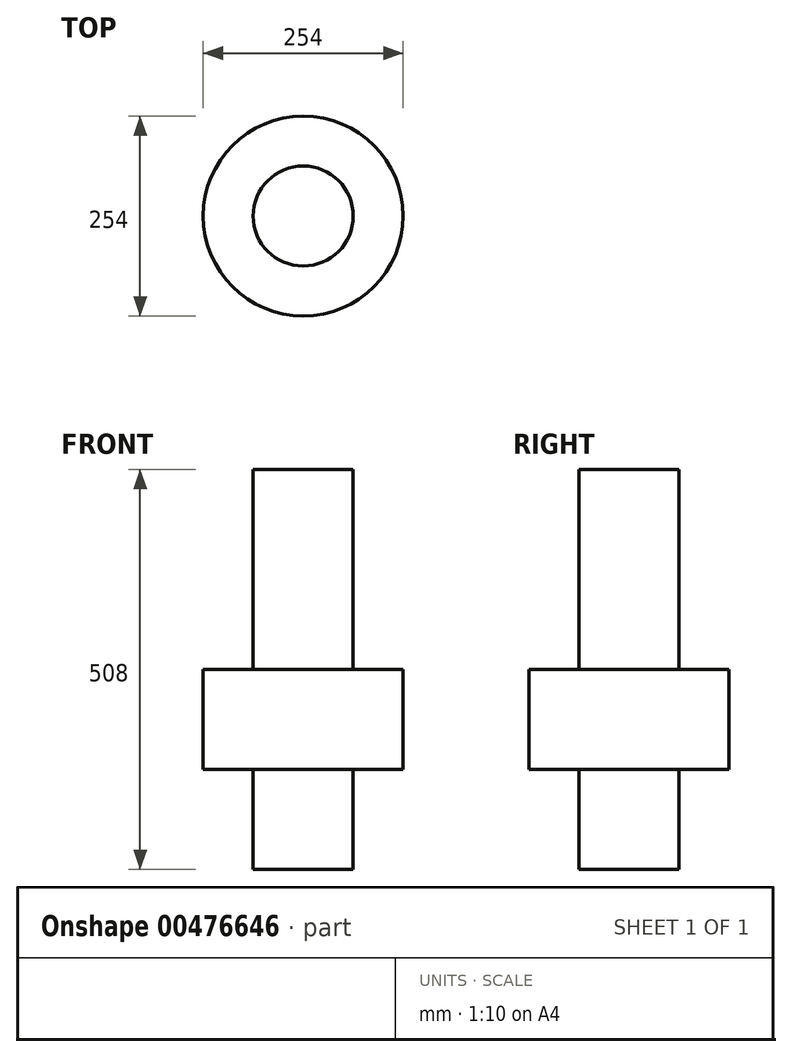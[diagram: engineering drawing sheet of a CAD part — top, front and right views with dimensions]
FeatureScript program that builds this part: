
annotation { "Feature Type Name" : "Feature", "Feature Type Description" : "" }
export const myFeature = defineFeature(function(context is Context, id is Id, definition is map)
    precondition{}
    {
        {
            var Q0;
            Q0=qCreatedBy(makeId("Top.planeOp"),FACE);
            var sketch = newSketch(context, id + "F0", { "sketchPlane" : qUnion([Q0])});
            skCircle(sketch, "E0", {"center": v(0, 0) * mm, "radius": 63.5 * mm});
            skSolve(sketch);
        }
        {
            var Q0;
            Q0=makeQuery(id+"F0.imprint","IMPRINT",FACE,{"disambiguationData":[TD([[makeQuery(id+"F0.imprint","IMPRINT",EDGE,{"derivedFrom":sQuery(id+"F0.wireOp",EDGE,"E0")}),1.0]])]});
            extrude(context, id + "F1", {"entities" : qUnion([Q0]), "depth" : 508 * mm});
        }
        {
            var Q0;
            Q0=makeQuery(id+"F1.opExtrude","CAP_FACE",FACE,{"disambiguationData":[OSD([sQuery(id+"F0.wireOp",EDGE,"E0")])],"isStart":true});
            cPlane(context, id + "F2", {"entities" : qUnion([Q0]), "cplaneType" : CPlaneType.OFFSET, "offset" : 127 * mm, "oppositeDirection" : true, "width" : 152.4 * mm, "height" : 152.4 * mm});
        }
        {
            var Q0;
            Q0=qCreatedBy(id+"F2.planeOp",FACE);
            var sketch = newSketch(context, id + "F3", { "sketchPlane" : qUnion([Q0])});
            skCircle(sketch, "E1.0.0", {"center": v(0, 0) * mm, "radius": 63.5 * mm, "construction": true});
            skCircle(sketch, "E2", {"center": v(0, 0) * mm, "radius": 127 * mm});
            skSolve(sketch);
        }
        {
            var Q0;
            Q0=makeQuery(id+"F3.imprint","IMPRINT",FACE,{"disambiguationData":[TD([[makeQuery(id+"F3.imprint","IMPRINT",EDGE,{"derivedFrom":sQuery(id+"F3.wireOp",EDGE,"E2")}),1.0]])]});
            extrude(context, id + "F4", {"entities" : qUnion([Q0]), "operationType" : NewBodyOperationType.ADD, "oppositeDirection" : true, "depth" : 127 * mm});
        }
    });
